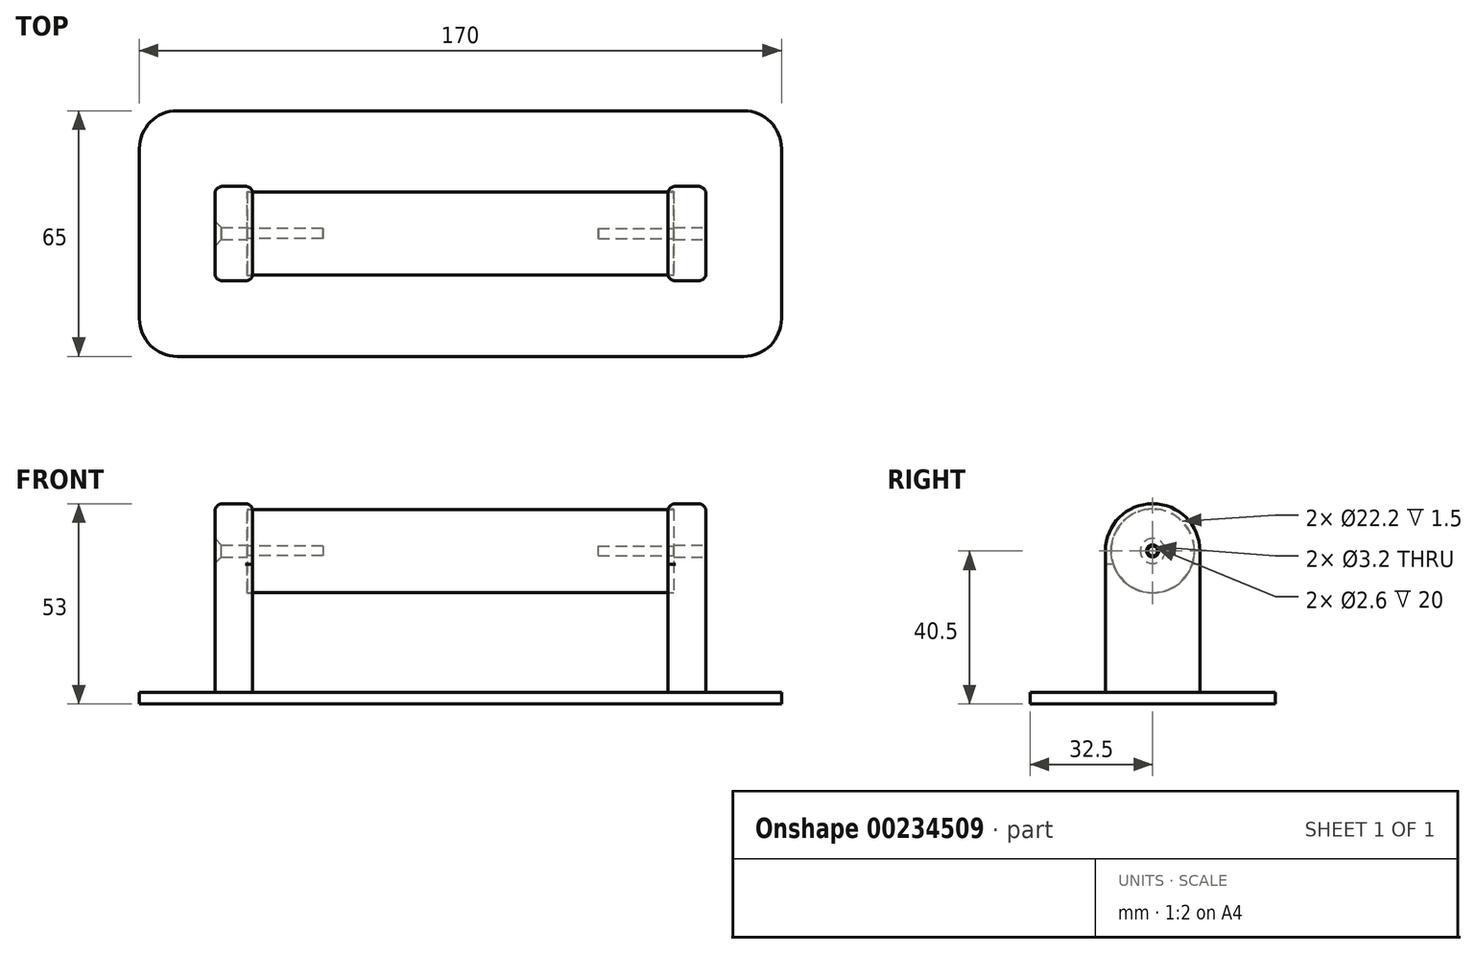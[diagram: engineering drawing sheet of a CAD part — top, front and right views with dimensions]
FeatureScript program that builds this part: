
annotation { "Feature Type Name" : "Feature", "Feature Type Description" : "" }
export const myFeature = defineFeature(function(context is Context, id is Id, definition is map)
    precondition{}
    {
        {
            var Q0;
            Q0=qCreatedBy(makeId("Top.planeOp"),FACE);
            var sketch = newSketch(context, id + "F0", { "sketchPlane" : qUnion([Q0])});
            skLineSegment(sketch, "E0.bottom", {"start": v(75, -32.5) * mm, "end": v(-75, -32.5) * mm});
            skLineSegment(sketch, "E0.top", {"start": v(75, 32.5) * mm, "end": v(-75, 32.5) * mm});
            skLineSegment(sketch, "E0.left", {"start": v(85, -22.5) * mm, "end": v(85, 22.5) * mm});
            skLineSegment(sketch, "E0.right", {"start": v(-85, -22.5) * mm, "end": v(-85, 22.5) * mm});
            skPoint(sketch, "E0.middle", {"position": v(0, 0) * mm});
            skPoint(sketch, "E1.visualSharp", {"position": v(-85, 32.5) * mm});
            skArc(sketch, "E1.filletArc", {"start": v(-75, 32.5) * mm, "mid": v(-82.07, 29.57) * mm, "end": v(-85, 22.5) * mm});
            skPoint(sketch, "E2.visualSharp", {"position": v(85, 32.5) * mm});
            skArc(sketch, "E2.filletArc", {"start": v(85, 22.5) * mm, "mid": v(82.07, 29.57) * mm, "end": v(75, 32.5) * mm});
            skPoint(sketch, "E3.visualSharp", {"position": v(85, -32.5) * mm});
            skArc(sketch, "E3.filletArc", {"start": v(75, -32.5) * mm, "mid": v(82.07, -29.57) * mm, "end": v(85, -22.5) * mm});
            skPoint(sketch, "E4.visualSharp", {"position": v(-85, -32.5) * mm});
            skArc(sketch, "E4.filletArc", {"start": v(-85, -22.5) * mm, "mid": v(-82.07, -29.57) * mm, "end": v(-75, -32.5) * mm});
            skSolve(sketch);
        }
        {
            var Q0;
            Q0 = qSketchRegion(id + "F0", true);
            extrude(context, id + "F1", {"entities" : qUnion([Q0]), "depth" : 3 * mm});
        }
        {
            var Q0;
            Q0=makeQuery(id+"F1.opExtrude","CAP_FACE",FACE,{"disambiguationData":[OSD([sQuery(id+"F0.wireOp",EDGE,"E0.bottom"),sQuery(id+"F0.wireOp",EDGE,"E0.top"),sQuery(id+"F0.wireOp",EDGE,"E0.left"),sQuery(id+"F0.wireOp",EDGE,"E0.right"),sQuery(id+"F0.wireOp",EDGE,"E1.filletArc"),sQuery(id+"F0.wireOp",EDGE,"E2.filletArc"),sQuery(id+"F0.wireOp",EDGE,"E3.filletArc"),sQuery(id+"F0.wireOp",EDGE,"E4.filletArc")])],"isStart":false});
            var sketch = newSketch(context, id + "F2", { "sketchPlane" : qUnion([Q0])});
            skLineSegment(sketch, "E5.bottom", {"start": v(-65, 12.5) * mm, "end": v(-55, 12.5) * mm});
            skLineSegment(sketch, "E5.top", {"start": v(-65, -12.5) * mm, "end": v(-55, -12.5) * mm});
            skLineSegment(sketch, "E5.left", {"start": v(-65, 12.5) * mm, "end": v(-65, -12.5) * mm});
            skLineSegment(sketch, "E5.right", {"start": v(-55, 12.5) * mm, "end": v(-55, -12.5) * mm});
            skPoint(sketch, "E5.middle", {"position": v(-60, 0) * mm});
            skLineSegment(sketch, "E6.MirrorCS", {"start": v(55, 12.5) * mm, "end": v(55, -12.5) * mm});
            skLineSegment(sketch, "E7.MirrorCS", {"start": v(65, 12.5) * mm, "end": v(65, -12.5) * mm});
            skLineSegment(sketch, "E8.MirrorCS", {"start": v(65, -12.5) * mm, "end": v(55, -12.5) * mm});
            skLineSegment(sketch, "E9.MirrorCS", {"start": v(65, 12.5) * mm, "end": v(55, 12.5) * mm});
            skPoint(sketch, "E10.MirrorP", {"position": v(60, 0) * mm});
            skSolve(sketch);
        }
        {
            var Q0;
            Q0 = qSketchRegion(id + "F2", true);
            extrude(context, id + "F3", {"entities" : qUnion([Q0]), "operationType" : NewBodyOperationType.ADD, "depth" : 50 * mm});
        }
        {
            var Q0;
            Q0=makeQuery(id+"F3.opExtrude","CAP_EDGE",EDGE,{"disambiguationData":[OSD([sQuery(id+"F2.wireOp",EDGE,"E5.bottom")])],"isStart":false});
            var Q1;
            Q1=makeQuery(id+"F3.opExtrude","CAP_EDGE",EDGE,{"disambiguationData":[OSD([sQuery(id+"F2.wireOp",EDGE,"E5.top")])],"isStart":false});
            var Q2;
            Q2=makeQuery(id+"F3.opExtrude","CAP_EDGE",EDGE,{"disambiguationData":[OSD([sQuery(id+"F2.wireOp",EDGE,"E9.MirrorCS")])],"isStart":false});
            var Q3;
            Q3=makeQuery(id+"F3.opExtrude","CAP_EDGE",EDGE,{"disambiguationData":[OSD([sQuery(id+"F2.wireOp",EDGE,"E8.MirrorCS")])],"isStart":false});
            fillet(context, id + "F4", {"entities" : qUnion([Q0, Q1, Q2, Q3]), "radius" : 12.5 * mm, "tangentPropagation" : true, "allowEdgeOverflow" : false});
        }
        {
            var Q0;
            Q0=makeQuery(id+"F3.opExtrude","SWEPT_FACE",FACE,{"disambiguationData":[OSD([sQuery(id+"F2.wireOp",EDGE,"E5.right")])]});
            var sketch = newSketch(context, id + "F5", { "sketchPlane" : qUnion([Q0])});
            skCircle(sketch, "E11", {"center": v(0, 40.5) * mm, "radius": 11.1 * mm});
            skSolve(sketch);
        }
        {
            var Q0;
            Q0 = qSketchRegion(id + "F5", true);
            extrude(context, id + "F6", {"entities" : qUnion([Q0]), "operationType" : NewBodyOperationType.REMOVE, "oppositeDirection" : true, "depth" : 1.5 * mm});
        }
        {
            var Q0;
            Q0=makeQuery(id+"F3.opExtrude","SWEPT_FACE",FACE,{"disambiguationData":[OSD([sQuery(id+"F2.wireOp",EDGE,"E6.MirrorCS")])]});
            var sketch = newSketch(context, id + "F7", { "sketchPlane" : qUnion([Q0])});
            skCircle(sketch, "E12", {"center": v(0, 40.5) * mm, "radius": 11.1 * mm});
            skSolve(sketch);
        }
        {
            var Q0;
            Q0 = qSketchRegion(id + "F7", true);
            extrude(context, id + "F8", {"entities" : qUnion([Q0]), "operationType" : NewBodyOperationType.REMOVE, "oppositeDirection" : true, "depth" : 1.5 * mm});
        }
        {
            var Q0;
            Q0=makeQuery(id+"F3.opExtrude","SWEPT_FACE",FACE,{"disambiguationData":[OSD([sQuery(id+"F2.wireOp",EDGE,"E7.MirrorCS")])]});
            var sketch = newSketch(context, id + "F9", { "sketchPlane" : qUnion([Q0])});
            skCircle(sketch, "E13", {"center": v(0, 40.5) * mm, "radius": 1.6 * mm});
            skSolve(sketch);
        }
        {
            var Q0;
            Q0 = qSketchRegion(id + "F9", true);
            extrude(context, id + "F10", {"entities" : qUnion([Q0]), "operationType" : NewBodyOperationType.REMOVE, "endBound" : BoundingType.THROUGH_ALL, "oppositeDirection" : true, "depth" : 25 * mm});
        }
        {
            var Q0;
            Q0=makeQuery(id+"F10.boolean.opBoolean","COPY",EDGE,{"derivedFrom":makeQuery(id+"F10.opExtrude","CAP_EDGE",EDGE,{"disambiguationData":[OSD([sQuery(id+"F9.wireOp",EDGE,"E13")])],"isStart":true})});
            var Q1;
            Q1=makeQuery(id+"F10.boolean.opBoolean","INTERSECT",EDGE,{"derivedFrom":[makeQuery(id+"F3.opExtrude","SWEPT_FACE",FACE,{"disambiguationData":[OSD([sQuery(id+"F2.wireOp",EDGE,"E5.left")])]}),makeQuery(id+"F10.opExtrude","SWEPT_FACE",FACE,{"disambiguationData":[OSD([sQuery(id+"F9.wireOp",EDGE,"E13")])]})]});
            chamfer(context, id + "F11", {"entities" : qUnion([Q0, Q1]), "width" : 1.7 * mm, "tangentPropagation" : true});
        }
        {
            var Q0;
            Q0=makeQuery(id+"F4.opFillet","BLEND_EDGE",EDGE,{"blendedFrom":[makeQuery(id+"F3.opExtrude","CAP_EDGE",EDGE,{"disambiguationData":[OSD([sQuery(id+"F2.wireOp",EDGE,"E5.bottom")])],"isStart":false}),makeQuery(id+"F3.opExtrude","SWEPT_FACE",FACE,{"disambiguationData":[OSD([sQuery(id+"F2.wireOp",EDGE,"E5.left")])]})],"blendedInto":[makeQuery(id+"F3.opExtrude","SWEPT_FACE",FACE,{"disambiguationData":[OSD([sQuery(id+"F2.wireOp",EDGE,"E5.left")])]})]});
            var Q1;
            Q1=makeQuery(id+"F4.opFillet","BLEND_EDGE",EDGE,{"blendedFrom":[makeQuery(id+"F3.opExtrude","CAP_EDGE",EDGE,{"disambiguationData":[OSD([sQuery(id+"F2.wireOp",EDGE,"E5.bottom")])],"isStart":false}),makeQuery(id+"F3.opExtrude","SWEPT_FACE",FACE,{"disambiguationData":[OSD([sQuery(id+"F2.wireOp",EDGE,"E5.right")])]})],"blendedInto":[makeQuery(id+"F3.opExtrude","SWEPT_FACE",FACE,{"disambiguationData":[OSD([sQuery(id+"F2.wireOp",EDGE,"E5.right")])]})]});
            var Q2;
            Q2=makeQuery(id+"F4.opFillet","BLEND_EDGE",EDGE,{"blendedFrom":[makeQuery(id+"F3.opExtrude","CAP_EDGE",EDGE,{"disambiguationData":[OSD([sQuery(id+"F2.wireOp",EDGE,"E8.MirrorCS")])],"isStart":false}),makeQuery(id+"F3.opExtrude","SWEPT_FACE",FACE,{"disambiguationData":[OSD([sQuery(id+"F2.wireOp",EDGE,"E6.MirrorCS")])]})],"blendedInto":[makeQuery(id+"F3.opExtrude","SWEPT_FACE",FACE,{"disambiguationData":[OSD([sQuery(id+"F2.wireOp",EDGE,"E6.MirrorCS")])]})]});
            var Q3;
            Q3=makeQuery(id+"F4.opFillet","BLEND_EDGE",EDGE,{"blendedFrom":[makeQuery(id+"F3.opExtrude","CAP_EDGE",EDGE,{"disambiguationData":[OSD([sQuery(id+"F2.wireOp",EDGE,"E8.MirrorCS")])],"isStart":false}),makeQuery(id+"F3.opExtrude","SWEPT_FACE",FACE,{"disambiguationData":[OSD([sQuery(id+"F2.wireOp",EDGE,"E7.MirrorCS")])]})],"blendedInto":[makeQuery(id+"F3.opExtrude","SWEPT_FACE",FACE,{"disambiguationData":[OSD([sQuery(id+"F2.wireOp",EDGE,"E7.MirrorCS")])]})]});
            var Q4;
            Q4=makeQuery(id+"F3.opExtrude","CAP_EDGE",EDGE,{"disambiguationData":[OSD([sQuery(id+"F2.wireOp",EDGE,"E5.right")])],"isStart":true});
            var Q5;
            Q5=makeQuery(id+"F3.opExtrude","CAP_EDGE",EDGE,{"disambiguationData":[OSD([sQuery(id+"F2.wireOp",EDGE,"E7.MirrorCS")])],"isStart":true});
            fillet(context, id + "F12", {"entities" : qUnion([Q0, Q1, Q2, Q3, Q4, Q5]), "radius" : 2 * mm, "tangentPropagation" : true, "allowEdgeOverflow" : false});
        }
        {
            var Q0;
            Q0=makeQuery(id+"F8.boolean.opBoolean","COPY",FACE,{"derivedFrom":makeQuery(id+"F8.opExtrude","CAP_FACE",FACE,{"disambiguationData":[OSD([sQuery(id+"F7.wireOp",EDGE,"E12")])],"isStart":false})});
            var sketch = newSketch(context, id + "F13", { "sketchPlane" : qUnion([Q0])});
            skCircle(sketch, "E14", {"center": v(0, 40.5) * mm, "radius": 11 * mm});
            skSolve(sketch);
        }
        {
            var Q0;
            Q0 = qSketchRegion(id + "F13", true);
            extrude(context, id + "F14", {"entities" : qUnion([Q0]), "depth" : 112.9 * mm});
        }
        {
            var Q0;
            Q0=makeQuery(id+"F14.opExtrude","CAP_FACE",FACE,{"disambiguationData":[OSD([sQuery(id+"F13.wireOp",EDGE,"E14")])],"isStart":true});
            var sketch = newSketch(context, id + "F15", { "sketchPlane" : qUnion([Q0])});
            skCircle(sketch, "E15", {"center": v(0, 40.5) * mm, "radius": 1.3 * mm});
            skSolve(sketch);
        }
        {
            var Q0;
            Q0 = qSketchRegion(id + "F15", true);
            extrude(context, id + "F16", {"entities" : qUnion([Q0]), "operationType" : NewBodyOperationType.REMOVE, "oppositeDirection" : true, "depth" : 20 * mm});
        }
        {
            var Q0;
            Q0=makeQuery(id+"F14.opExtrude","CAP_FACE",FACE,{"disambiguationData":[OSD([sQuery(id+"F13.wireOp",EDGE,"E14")])],"isStart":false});
            var sketch = newSketch(context, id + "F17", { "sketchPlane" : qUnion([Q0])});
            skCircle(sketch, "E16", {"center": v(0, 40.5) * mm, "radius": 1.3 * mm});
            skSolve(sketch);
        }
        {
            var Q0;
            Q0 = qSketchRegion(id + "F17", true);
            extrude(context, id + "F18", {"entities" : qUnion([Q0]), "operationType" : NewBodyOperationType.REMOVE, "oppositeDirection" : true, "depth" : 20 * mm});
        }
    });
